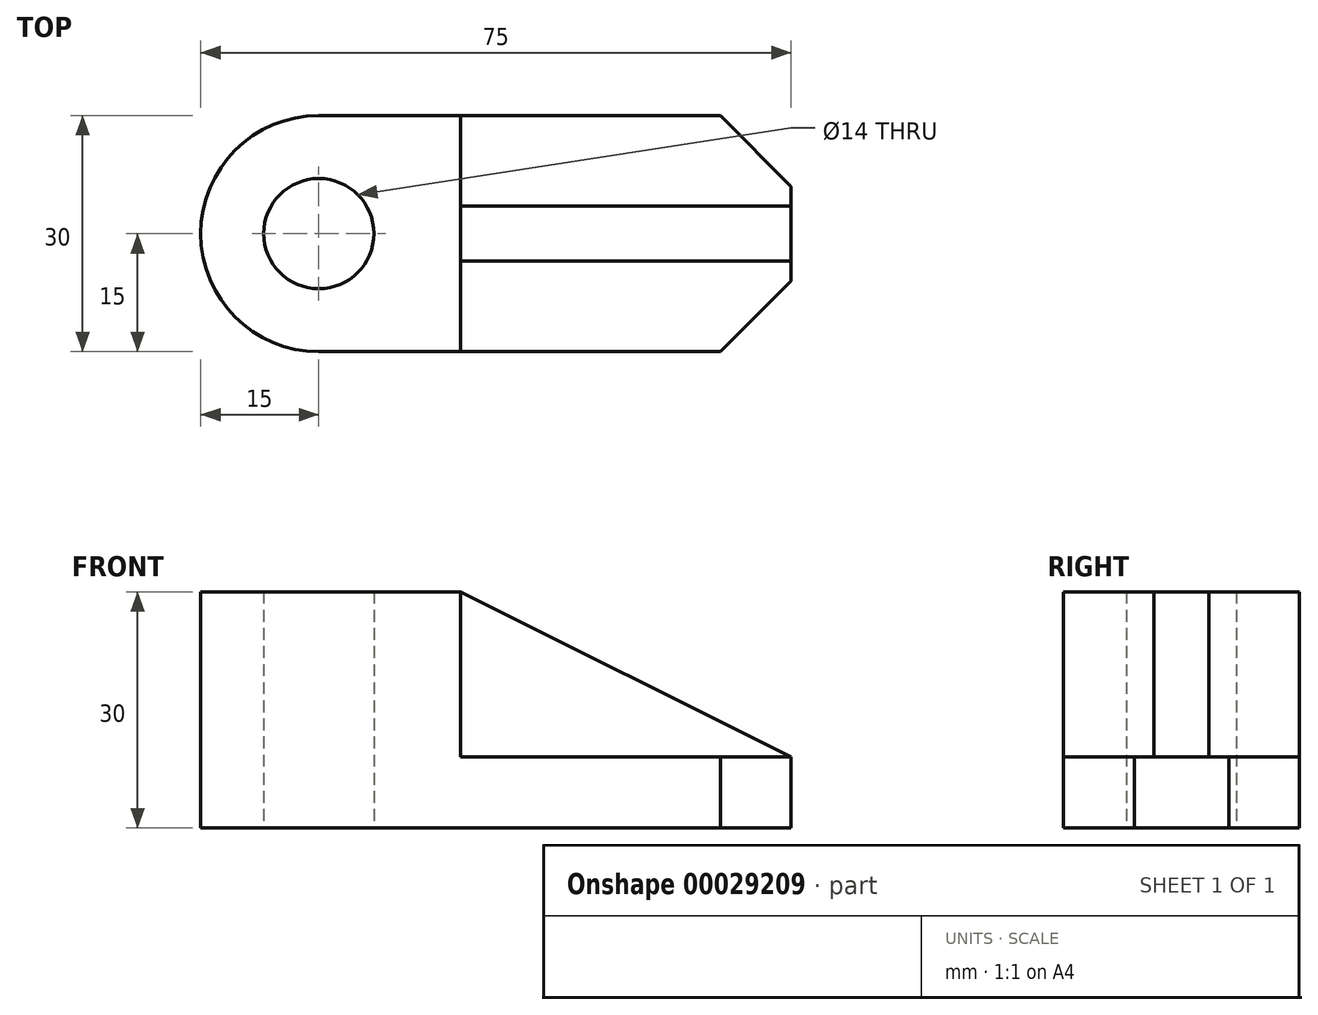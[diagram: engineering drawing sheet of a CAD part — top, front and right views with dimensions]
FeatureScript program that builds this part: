
annotation { "Feature Type Name" : "Feature", "Feature Type Description" : "" }
export const myFeature = defineFeature(function(context is Context, id is Id, definition is map)
    precondition{}
    {
        {
            var Q0;
            Q0=qCreatedBy(makeId("Top.planeOp"),FACE);
            var sketch = newSketch(context, id + "F0", { "sketchPlane" : qUnion([Q0])});
            skLineSegment(sketch, "E0.rect.bottom", {"start": v(21, -15) * mm, "end": v(-30, -15) * mm});
            skLineSegment(sketch, "E0.rect.top", {"start": v(21, 15) * mm, "end": v(-30, 15) * mm});
            skLineSegment(sketch, "E0.rect.left", {"start": v(30, -6) * mm, "end": v(30, 6) * mm});
            skPoint(sketch, "E0.rect.middle", {"position": v(0, 0) * mm});
            skLineSegment(sketch, "E1", {"start": v(21, 15) * mm, "end": v(30, 6) * mm});
            skLineSegment(sketch, "E2.MirrorCS", {"start": v(21, -15) * mm, "end": v(30, -6) * mm});
            skPoint(sketch, "E3.orphan", {"position": v(30, 15) * mm});
            skPoint(sketch, "E4.orphan", {"position": v(30, -15) * mm});
            skArc(sketch, "E5", {"start": v(-30, 15) * mm, "mid": v(-45, 0) * mm, "end": v(-30, -15) * mm});
            skCircle(sketch, "E6", {"center": v(-30, 0) * mm, "radius": 7 * mm});
            skLineSegment(sketch, "E7", {"start": v(-12, 15) * mm, "end": v(-12, -15) * mm});
            skSolve(sketch);
        }
        {
            var Q0;
            {var subQ1=sQuery(id+"F0.wireOp",EDGE,"E5");Q0=makeQuery(id+"F0.imprint","IMPRINT",FACE,{"disambiguationData":[TD([[makeQuery(id+"F0.imprint","IMPRINT",EDGE,{"derivedFrom":subQ1}),1.0]])]});}
            extrude(context, id + "F1", {"entities" : qUnion([Q0]), "oppositeDirection" : true, "depth" : 30 * mm});
        }
        {
            var Q0;
            Q0 = qSketchRegion(id + "F0", true);
            extrude(context, id + "F2", {"entities" : qUnion([Q0]), "operationType" : NewBodyOperationType.ADD, "oppositeDirection" : true, "depth" : 9 * mm});
        }
        {
            var Q0;
            Q0=makeQuery(id+"F2.opExtrude","CAP_FACE",FACE,{"disambiguationData":[OSD([sQuery(id+"F0.wireOp",EDGE,"E0.rect.bottom"),sQuery(id+"F0.wireOp",EDGE,"E0.rect.top"),sQuery(id+"F0.wireOp",EDGE,"E0.rect.left"),sQuery(id+"F0.wireOp",EDGE,"E1"),sQuery(id+"F0.wireOp",EDGE,"E2.MirrorCS"),sQuery(id+"F0.wireOp",EDGE,"E5"),sQuery(id+"F0.wireOp",EDGE,"E6")])],"isStart":false});
            var sketch = newSketch(context, id + "F3", { "sketchPlane" : qUnion([Q0])});
            skLineSegment(sketch, "E8", {"start": v(30, 3.5) * mm, "end": v(-12, 3.5) * mm});
            skLineSegment(sketch, "E9", {"start": v(30, -3.5) * mm, "end": v(-12, -3.5) * mm});
            skPoint(sketch, "E10.start.orphan", {"position": v(30, 6) * mm});
            skPoint(sketch, "E11.start.orphan", {"position": v(30, -6) * mm});
            skSolve(sketch);
        }
        {
            var Q0;
            {var subQ3=sQuery(id+"F3.wireOp",EDGE,"E8");Q0=makeQuery(id+"F3.imprint","IMPRINT",FACE,{"disambiguationData":[TD([[makeQuery(id+"F3.imprint","IMPRINT",EDGE,{"derivedFrom":subQ3}),1.0]])]});}
            extrude(context, id + "F4", {"entities" : qUnion([Q0]), "operationType" : NewBodyOperationType.ADD, "depth" : 21 * mm});
        }
        {
            var Q0;
            Q0=makeQuery(id+"F4.opExtrude","SWEPT_FACE",FACE,{"disambiguationData":[OSD([sQuery(id+"F3.wireOp",EDGE,"E8")])]});
            var sketch = newSketch(context, id + "F5", { "sketchPlane" : qUnion([Q0])});
            skLineSegment(sketch, "E12", {"start": v(-12, -30) * mm, "end": v(30, -9) * mm});
            skSolve(sketch);
        }
        {
            var Q0;
            Q0 = qSketchRegion(id + "F5", true);
            var Q1;
            Q1=makeQuery(id+"F5.imprint","IMPRINT",FACE,{"disambiguationData":[TD([[makeQuery(id+"F5.imprint","IMPRINT",EDGE,{"derivedFrom":sQuery(id+"F5.wireOp",EDGE,"E12")}),-1.0]])]});
            extrude(context, id + "F6", {"entities" : qUnion([Q0, Q1]), "operationType" : NewBodyOperationType.REMOVE, "oppositeDirection" : true, "depth" : 25 * mm});
        }
        {
            var Q0;
            Q0=makeQuery(id+"F1.opExtrude","SWEPT_BODY",BODY,{"disambiguationData":[OSD([sQuery(id+"F0.wireOp",EDGE,"E0.rect.bottom"),sQuery(id+"F0.wireOp",EDGE,"E0.rect.top"),sQuery(id+"F0.wireOp",EDGE,"E5"),sQuery(id+"F0.wireOp",EDGE,"E6"),sQuery(id+"F0.wireOp",EDGE,"E7")])]});
            var Q1;
            {var subQ0=sQuery(id+"F0.wireOp",EDGE,"E0.rect.bottom");Q1=makeQuery(id+"F2.boolean.opBoolean","MERGE",FACE,{"derivedFrom":[makeQuery(id+"F1.opExtrude","SWEPT_FACE",FACE,{"disambiguationData":[OSD([subQ0])]}),makeQuery(id+"F2.opExtrude","SWEPT_FACE",FACE,{"disambiguationData":[OSD([subQ0])]})]});}
            mirror(context, id + "F7", {"operationType" : NewBodyOperationType.REMOVE, "entities" : qUnion([Q0]), "mirrorPlane" : qUnion([Q1])});
        }
        {
            var Q0;
            Q0=makeQuery(id+"F1.opExtrude","SWEPT_BODY",BODY,{"disambiguationData":[OSD([sQuery(id+"F0.wireOp",EDGE,"E0.rect.bottom"),sQuery(id+"F0.wireOp",EDGE,"E0.rect.top"),sQuery(id+"F0.wireOp",EDGE,"E5"),sQuery(id+"F0.wireOp",EDGE,"E6"),sQuery(id+"F0.wireOp",EDGE,"E7")])]});
            var Q1;
            Q1=qCreatedBy(makeId("Top.planeOp"),FACE);
            mirror(context, id + "F8", {"entities" : qUnion([Q0]), "mirrorPlane" : qUnion([Q1])});
        }
        {
            var Q0;
            Q0=makeQuery(id+"F1.opExtrude","SWEPT_BODY",BODY,{"disambiguationData":[OSD([sQuery(id+"F0.wireOp",EDGE,"E0.rect.bottom"),sQuery(id+"F0.wireOp",EDGE,"E0.rect.top"),sQuery(id+"F0.wireOp",EDGE,"E5"),sQuery(id+"F0.wireOp",EDGE,"E6"),sQuery(id+"F0.wireOp",EDGE,"E7")])]});
            deleteBodies(context, id + "F9", {"entities" : qUnion([Q0])});
        }
    });
